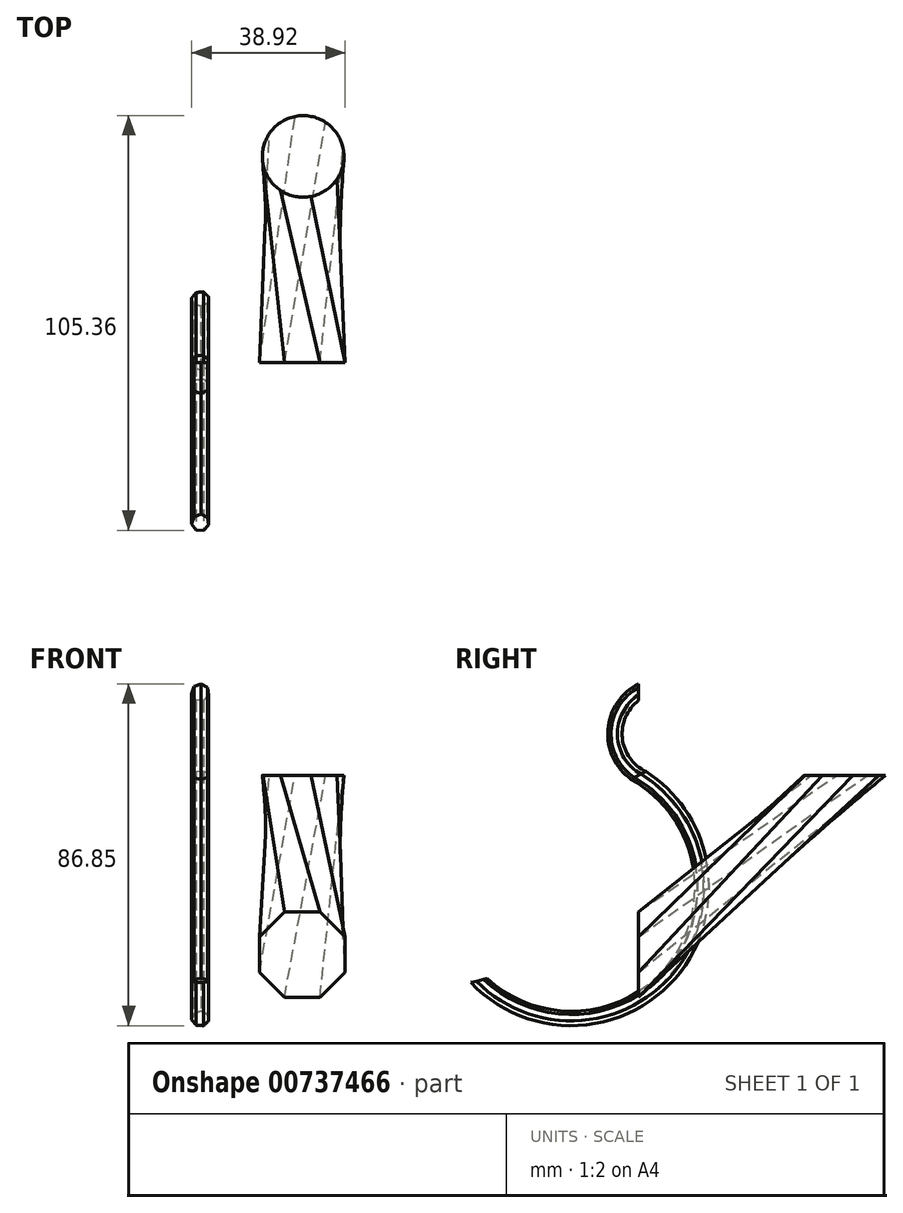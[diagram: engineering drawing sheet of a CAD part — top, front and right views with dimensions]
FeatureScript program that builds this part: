
annotation { "Feature Type Name" : "Feature", "Feature Type Description" : "" }
export const myFeature = defineFeature(function(context is Context, id is Id, definition is map)
    precondition{}
    {
        {
            var Q0;
            Q0=qCreatedBy(makeId("Right.planeOp"),FACE);
            var sketch = newSketch(context, id + "F0", { "sketchPlane" : qUnion([Q0])});
            skArc(sketch, "E0", {"start": v(-40.6, -52.12) * mm, "mid": v(9.1, -48.95) * mm, "end": v(0, 0) * mm});
            skArc(sketch, "E1", {"start": v(0, 21.1) * mm, "mid": v(-5.96, 10.55) * mm, "end": v(0, 0) * mm});
            skSolve(sketch);
        }
        {
            var Q0;
            Q0=qCreatedBy(makeId("Front.planeOp"),FACE);
            var sketch = newSketch(context, id + "F1", { "sketchPlane" : qUnion([Q0])});
            skCircle(sketch, "E2.cCircle", {"center": v(0, 21.05) * mm, "radius": 2 * mm, "construction": true});
            skLineSegment(sketch, "E2.0", {"start": v(2.12, 20.42) * mm, "end": v(0.83, 19) * mm});
            skLineSegment(sketch, "E2.1", {"start": v(0.83, 19) * mm, "end": v(-1.08, 19.12) * mm});
            skLineSegment(sketch, "E2.2", {"start": v(-1.08, 19.12) * mm, "end": v(-2.18, 20.7) * mm});
            skLineSegment(sketch, "E2.3", {"start": v(-2.18, 20.7) * mm, "end": v(-1.64, 22.53) * mm});
            skLineSegment(sketch, "E2.4", {"start": v(-1.64, 22.53) * mm, "end": v(0.14, 23.26) * mm});
            skLineSegment(sketch, "E2.5", {"start": v(0.14, 23.26) * mm, "end": v(1.81, 22.32) * mm});
            skLineSegment(sketch, "E2.6", {"start": v(1.81, 22.32) * mm, "end": v(2.12, 20.42) * mm});
            skPoint(sketch, "E2.0.midPoint", {"position": v(1.48, 19.71) * mm});
            skSolve(sketch);
        }
        {
            var Q0;
            Q0=makeQuery(id+"F1.imprint","IMPRINT",FACE,{"disambiguationData":[TD([[makeQuery(id+"F1.imprint","IMPRINT",EDGE,{"derivedFrom":sQuery(id+"F1.wireOp",EDGE,"E2.0")}),-1.0]])]});
            var Q1;
            Q1=sQuery(id+"F0.wireOp",EDGE,"E1");
            var Q2;
            Q2=sQuery(id+"F0.wireOp",EDGE,"E0");
            sweep(context, id + "F2", {"profiles" : qUnion([Q0]), "path" : qUnion([Q1, Q2])});
        }
        {
            var Q0;
            Q0=qCreatedBy(makeId("Top.planeOp"),FACE);
            var sketch = newSketch(context, id + "F3", { "sketchPlane" : qUnion([Q0])});
            skCircle(sketch, "E3", {"center": v(26.1, 52.38) * mm, "radius": 10.36 * mm});
            skSolve(sketch);
        }
        {
            var Q0;
            Q0=qCreatedBy(makeId("Front.planeOp"),FACE);
            var sketch = newSketch(context, id + "F4", { "sketchPlane" : qUnion([Q0])});
            skCircle(sketch, "E4.cCircle", {"center": v(25.87, -45.52) * mm, "radius": 10.87 * mm, "construction": true});
            skLineSegment(sketch, "E4.0", {"start": v(36.74, -41.02) * mm, "end": v(36.74, -50.03) * mm});
            skLineSegment(sketch, "E4.1", {"start": v(36.74, -50.03) * mm, "end": v(30.37, -56.4) * mm});
            skLineSegment(sketch, "E4.2", {"start": v(30.37, -56.4) * mm, "end": v(21.37, -56.4) * mm});
            skLineSegment(sketch, "E4.3", {"start": v(21.37, -56.4) * mm, "end": v(15, -50.03) * mm});
            skLineSegment(sketch, "E4.4", {"start": v(15, -50.03) * mm, "end": v(15, -41.02) * mm});
            skLineSegment(sketch, "E4.5", {"start": v(15, -41.02) * mm, "end": v(21.37, -34.66) * mm});
            skLineSegment(sketch, "E4.6", {"start": v(21.37, -34.66) * mm, "end": v(30.37, -34.66) * mm});
            skLineSegment(sketch, "E4.7", {"start": v(30.37, -34.66) * mm, "end": v(36.74, -41.02) * mm});
            skPoint(sketch, "E4.0.midPoint", {"position": v(36.74, -45.52) * mm});
            skSolve(sketch);
        }
        {
            var Q0;
            Q0=makeQuery(id+"F4.imprint","IMPRINT",FACE,{"disambiguationData":[TD([[makeQuery(id+"F4.imprint","IMPRINT",EDGE,{"derivedFrom":sQuery(id+"F4.wireOp",EDGE,"E4.0")}),-1.0]])]});
            var Q1;
            Q1=makeQuery(id+"F3.imprint","IMPRINT",FACE,{"disambiguationData":[TD([[makeQuery(id+"F3.imprint","IMPRINT",EDGE,{"derivedFrom":sQuery(id+"F3.wireOp",EDGE,"E3")}),1.0]])]});
            loft(context, id + "F5", {"sheetProfilesArray" : [{ "sheetProfileEntities" : qUnion([Q0]) }, { "sheetProfileEntities" : qUnion([Q1]) }]});
        }
    });
